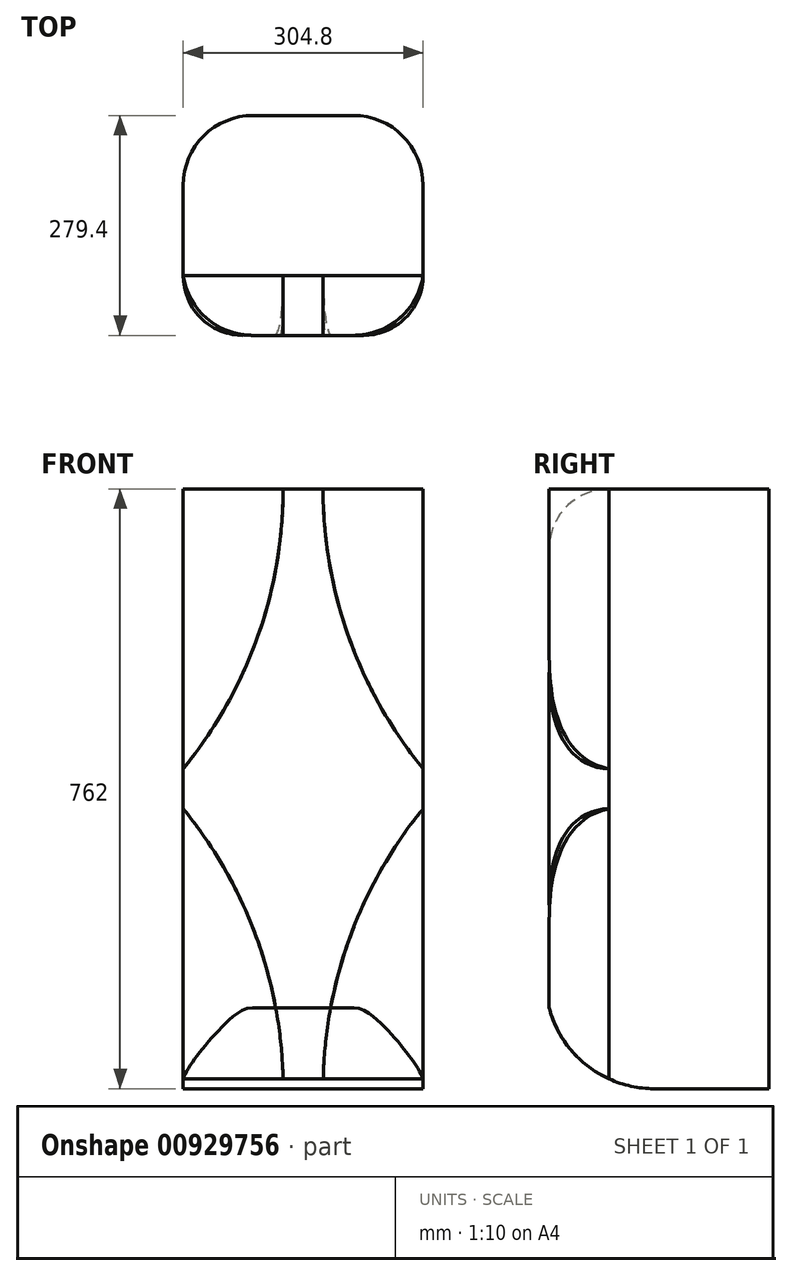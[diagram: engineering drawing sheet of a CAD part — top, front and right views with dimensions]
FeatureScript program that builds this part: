
annotation { "Feature Type Name" : "Feature", "Feature Type Description" : "" }
export const myFeature = defineFeature(function(context is Context, id is Id, definition is map)
    precondition{}
    {
        {
            var Q0;
            Q0=qCreatedBy(makeId("Front.planeOp"),FACE);
            var sketch = newSketch(context, id + "F0", { "sketchPlane" : qUnion([Q0])});
            skLineSegment(sketch, "E0.bottom", {"start": v(152.4, 381) * mm, "end": v(-152.4, 381) * mm});
            skLineSegment(sketch, "E0.top", {"start": v(152.4, -381) * mm, "end": v(-152.4, -381) * mm});
            skLineSegment(sketch, "E0.left", {"start": v(152.4, 381) * mm, "end": v(152.4, -381) * mm});
            skLineSegment(sketch, "E0.right", {"start": v(-152.4, 381) * mm, "end": v(-152.4, -381) * mm});
            skLineSegment(sketch, "E1", {"start": v(0, 0) * mm, "end": v(0, -381) * mm, "construction": true});
            skLineSegment(sketch, "E2.0", {"start": v(-25.4, 0) * mm, "end": v(-25.4, -381) * mm, "construction": true});
            skLineSegment(sketch, "E3", {"start": v(-152.4, 0) * mm, "end": v(152.4, 0) * mm});
            skLineSegment(sketch, "E4.0", {"start": v(-152.4, -25.4) * mm, "end": v(152.4, -25.4) * mm, "construction": true});
            skPoint(sketch, "E5", {"position": v(-25.4, -266.7) * mm});
            skArc(sketch, "E6", {"start": v(-25.4, -381) * mm, "mid": v(-58.1, -192.2) * mm, "end": v(-152.4, -25.4) * mm, "construction": true});
            skArc(sketch, "E7.MirrorCS", {"start": v(25.4, -381) * mm, "mid": v(58.1, -192.2) * mm, "end": v(152.4, -25.4) * mm, "construction": true});
            skArc(sketch, "E8.MirrorCS", {"start": v(25.4, 381) * mm, "mid": v(58.1, 192.2) * mm, "end": v(152.4, 25.4) * mm, "construction": true});
            skArc(sketch, "E9.MirrorCS", {"start": v(-25.4, 381) * mm, "mid": v(-58.1, 192.2) * mm, "end": v(-152.4, 25.4) * mm, "construction": true});
            skLineSegment(sketch, "E10.bottom", {"start": v(76.2, 101.6) * mm, "end": v(-76.2, 101.6) * mm, "construction": true});
            skLineSegment(sketch, "E10.top", {"start": v(76.2, -101.6) * mm, "end": v(-76.2, -101.6) * mm, "construction": true});
            skLineSegment(sketch, "E10.left", {"start": v(76.2, 101.6) * mm, "end": v(76.2, -101.6) * mm, "construction": true});
            skLineSegment(sketch, "E10.right", {"start": v(-76.2, 101.6) * mm, "end": v(-76.2, -101.6) * mm, "construction": true});
            skPoint(sketch, "E10.middle", {"position": v(0, 0) * mm});
            skSolve(sketch);
        }
        {
            var Q0;
            Q0=qCreatedBy(makeId("Top.planeOp"),FACE);
            var Q1;
            Q1=sQuery(id+"F0.wireOp",VERTEX,"E1.end");
            cPlane(context, id + "F1", {"entities" : qUnion([Q0, Q1]), "cplaneType" : CPlaneType.PLANE_POINT, "offset" : 25.4 * mm, "width" : 152.4 * mm, "height" : 152.4 * mm});
        }
        {
            var Q0;
            Q0=qCreatedBy(id+"F1.planeOp",FACE);
            var sketch = newSketch(context, id + "F2", { "sketchPlane" : qUnion([Q0])});
            skPoint(sketch, "E11.0", {"position": v(152.4, 0) * mm});
            skPoint(sketch, "E12.middle", {"position": v(0, 0) * mm});
            skPoint(sketch, "E13.0", {"position": v(-152.4, 0) * mm});
            skPoint(sketch, "E14.0", {"position": v(-25.4, 0) * mm});
            skPoint(sketch, "E15.0", {"position": v(25.4, 0) * mm});
            skLineSegment(sketch, "E16.bottom", {"start": v(-152.4, 0) * mm, "end": v(152.4, 0) * mm});
            skLineSegment(sketch, "E16.top", {"start": v(-152.4, 203.2) * mm, "end": v(152.4, 203.2) * mm});
            skLineSegment(sketch, "E16.left", {"start": v(-152.4, 0) * mm, "end": v(-152.4, 203.2) * mm});
            skLineSegment(sketch, "E16.right", {"start": v(152.4, 0) * mm, "end": v(152.4, 203.2) * mm});
            skLineSegment(sketch, "E17", {"start": v(0, 0) * mm, "end": v(0, 152.4) * mm, "construction": true});
            skSolve(sketch);
        }
        {
            var Q0;
            Q0 = qSketchRegion(id + "F2", true);
            var Q1;
            Q1=sQuery(id+"F0.wireOp",VERTEX,"E0.bottom.end");
            extrude(context, id + "F3", {"entities" : qUnion([Q0]), "endBound" : BoundingType.UP_TO_VERTEX, "depth" : 25.4 * mm, "endBoundEntityVertex" : qUnion([Q1]), "offsetDistance" : 25.4 * mm});
        }
        {
            var Q0;
            Q0=qCreatedBy(makeId("Top.planeOp"),FACE);
            var sketch = newSketch(context, id + "F4", { "sketchPlane" : qUnion([Q0])});
            skCircle(sketch, "E18.0", {"center": v(0, 0) * mm, "radius": 76.2 * mm, "construction": true});
            skLineSegment(sketch, "E19", {"start": v(0, 0) * mm, "end": v(0, -76.2) * mm, "construction": true});
            skPoint(sketch, "E20", {"position": v(0, -76.2) * mm});
            skSolve(sketch);
        }
        {
            var Q0;
            Q0=sQuery(id+"F4.wireOp",VERTEX,"E20");
            var Q1;
            Q1=qCreatedBy(makeId("Front.planeOp"),FACE);
            cPlane(context, id + "F5", {"entities" : qUnion([Q0, Q1]), "cplaneType" : CPlaneType.PLANE_POINT, "offset" : 25.4 * mm, "width" : 152.4 * mm, "height" : 152.4 * mm});
        }
        {
            var Q0;
            Q0=qCreatedBy(id+"F5.planeOp",FACE);
            var sketch = newSketch(context, id + "F6", { "sketchPlane" : qUnion([Q0])});
            skLineSegment(sketch, "E21.0", {"start": v(152.4, 381) * mm, "end": v(25.4, 381) * mm});
            skLineSegment(sketch, "E21.1", {"start": v(152.4, -381) * mm, "end": v(25.4, -381) * mm});
            skLineSegment(sketch, "E21.2", {"start": v(152.4, 381) * mm, "end": v(152.4, 25.4) * mm});
            skLineSegment(sketch, "E21.3", {"start": v(-152.4, 381) * mm, "end": v(-152.4, 25.4) * mm});
            skPoint(sketch, "E21.11", {"position": v(-25.4, -266.7) * mm});
            skArc(sketch, "E21.12", {"start": v(-25.4, -381) * mm, "mid": v(-58.1, -192.2) * mm, "end": v(-152.4, -25.4) * mm});
            skArc(sketch, "E21.13", {"start": v(25.4, -381) * mm, "mid": v(58.1, -192.2) * mm, "end": v(152.4, -25.4) * mm});
            skArc(sketch, "E21.14", {"start": v(25.4, 381) * mm, "mid": v(58.1, 192.2) * mm, "end": v(152.4, 25.4) * mm});
            skArc(sketch, "E21.15", {"start": v(-25.4, 381) * mm, "mid": v(-58.1, 192.2) * mm, "end": v(-152.4, 25.4) * mm});
            skLineSegment(sketch, "E21.16", {"start": v(76.2, 101.6) * mm, "end": v(-76.2, 101.6) * mm});
            skLineSegment(sketch, "E21.17", {"start": v(76.2, -101.6) * mm, "end": v(-76.2, -101.6) * mm});
            skLineSegment(sketch, "E21.18", {"start": v(76.2, 101.6) * mm, "end": v(76.2, -101.6) * mm});
            skLineSegment(sketch, "E21.19", {"start": v(-76.2, 101.6) * mm, "end": v(-76.2, -101.6) * mm});
            skPoint(sketch, "E21.20", {"position": v(0, 0) * mm});
            skLineSegment(sketch, "E22.trimOffspring", {"start": v(-25.4, 381) * mm, "end": v(-152.4, 381) * mm});
            skLineSegment(sketch, "E23.trimOffspring", {"start": v(-25.4, -381) * mm, "end": v(-152.4, -381) * mm});
            skLineSegment(sketch, "E24.trimOffspring", {"start": v(152.4, -25.4) * mm, "end": v(152.4, -381) * mm});
            skLineSegment(sketch, "E25.trimOffspring", {"start": v(-152.4, -25.4) * mm, "end": v(-152.4, -381) * mm});
            skSolve(sketch);
        }
        {
            var Q0;
            Q0=makeQuery(id+"F6.imprint","IMPRINT",FACE,{"disambiguationData":[TD([[makeQuery(id+"F6.imprint","IMPRINT",EDGE,{"derivedFrom":sQuery(id+"F6.wireOp",EDGE,"E21.3")}),1.0]])]});
            var Q1;
            Q1=makeQuery(id+"F6.imprint","IMPRINT",FACE,{"disambiguationData":[TD([[makeQuery(id+"F6.imprint","IMPRINT",EDGE,{"derivedFrom":sQuery(id+"F6.wireOp",EDGE,"E21.0")}),1.0]])]});
            var Q2;
            Q2=makeQuery(id+"F6.imprint","IMPRINT",FACE,{"disambiguationData":[TD([[makeQuery(id+"F6.imprint","IMPRINT",EDGE,{"derivedFrom":sQuery(id+"F6.wireOp",EDGE,"E21.1")}),-1.0]])]});
            var Q3;
            Q3=makeQuery(id+"F6.imprint","IMPRINT",FACE,{"disambiguationData":[TD([[makeQuery(id+"F6.imprint","IMPRINT",EDGE,{"derivedFrom":sQuery(id+"F6.wireOp",EDGE,"E21.12")}),1.0]])]});
            extrude(context, id + "F7", {"entities" : qUnion([Q0, Q1, Q2, Q3]), "endBound" : BoundingType.UP_TO_NEXT, "oppositeDirection" : true, "depth" : 25.4 * mm, "offsetDistance" : 25.4 * mm});
        }
        {
            var Q0;
            Q0=makeQuery(id+"F7.opExtrude","CAP_EDGE",EDGE,{"disambiguationData":[OSD([sQuery(id+"F6.wireOp",EDGE,"E21.2")])],"isStart":true});
            var Q1;
            Q1=makeQuery(id+"F7.opExtrude","CAP_EDGE",EDGE,{"disambiguationData":[OSD([sQuery(id+"F6.wireOp",EDGE,"E21.3")])],"isStart":true});
            var Q2;
            Q2=makeQuery(id+"F7.opExtrude","CAP_EDGE",EDGE,{"disambiguationData":[OSD([sQuery(id+"F6.wireOp",EDGE,"E25.trimOffspring")])],"isStart":true});
            var Q3;
            Q3=makeQuery(id+"F7.opExtrude","CAP_EDGE",EDGE,{"disambiguationData":[OSD([sQuery(id+"F6.wireOp",EDGE,"E24.trimOffspring")])],"isStart":true});
            var Q4;
            Q4=makeQuery(id+"F3.opExtrude","SWEPT_EDGE",EDGE,{"disambiguationData":[OSD([sQuery(id+"F2.wireOp",EDGE,"E16.top"),sQuery(id+"F2.wireOp",EDGE,"E16.right")])]});
            var Q5;
            Q5=makeQuery(id+"F3.opExtrude","SWEPT_EDGE",EDGE,{"disambiguationData":[OSD([sQuery(id+"F2.wireOp",EDGE,"E16.top"),sQuery(id+"F2.wireOp",EDGE,"E16.left")])]});
            fillet(context, id + "F8", {"entities" : qUnion([Q0, Q1, Q2, Q3, Q4, Q5]), "radius" : 88.9 * mm, "tangentPropagation" : true, "allowEdgeOverflow" : false});
        }
        {
            var Q0;
            Q0=makeQuery(id+"F3.opExtrude","SWEPT_FACE",FACE,{"disambiguationData":[OSD([sQuery(id+"F2.wireOp",EDGE,"E16.bottom")])]});
            var sketch = newSketch(context, id + "F9", { "sketchPlane" : qUnion([Q0])});
            skArc(sketch, "E26.0", {"start": v(-152.4, 25.4) * mm, "mid": v(-102.56, 96.97) * mm, "end": v(-64.41, 175.39) * mm});
            skArc(sketch, "E27.0", {"start": v(-25.4, 381) * mm, "mid": v(-35.24, 276.36) * mm, "end": v(-64.41, 175.39) * mm});
            skArc(sketch, "E28.0", {"start": v(25.4, 381) * mm, "mid": v(35.24, 276.36) * mm, "end": v(64.41, 175.39) * mm});
            skArc(sketch, "E29.0", {"start": v(64.41, 175.39) * mm, "mid": v(102.56, 96.97) * mm, "end": v(152.4, 25.4) * mm});
            skArc(sketch, "E30.0", {"start": v(152.4, -25.4) * mm, "mid": v(102.56, -96.97) * mm, "end": v(64.41, -175.39) * mm});
            skArc(sketch, "E31.0", {"start": v(25.4, -381) * mm, "mid": v(35.24, -276.36) * mm, "end": v(64.41, -175.39) * mm});
            skArc(sketch, "E32.0", {"start": v(-25.4, -381) * mm, "mid": v(-35.24, -276.36) * mm, "end": v(-64.41, -175.39) * mm});
            skArc(sketch, "E33.0", {"start": v(-64.41, -175.39) * mm, "mid": v(-102.56, -96.97) * mm, "end": v(-152.4, -25.4) * mm});
            skLineSegment(sketch, "E34", {"start": v(-152.4, 25.4) * mm, "end": v(-152.4, -25.4) * mm});
            skLineSegment(sketch, "E35", {"start": v(152.4, 25.4) * mm, "end": v(152.4, -25.4) * mm});
            skLineSegment(sketch, "E36", {"start": v(-25.4, 381) * mm, "end": v(25.4, 381) * mm});
            skLineSegment(sketch, "E37", {"start": v(-25.4, -381) * mm, "end": v(25.4, -381) * mm});
            skSolve(sketch);
        }
        {
            var Q0;
            Q0 = qSketchRegion(id + "F9", true);
            var Q1;
            Q1=makeQuery(id+"F7.opExtrude","CAP_VERTEX",VERTEX,{"disambiguationData":[OSD([sQuery(id+"F6.wireOp",EDGE,"E21.15"),sQuery(id+"F6.wireOp",EDGE,"E22.trimOffspring")])],"isStart":true});
            extrude(context, id + "F10", {"entities" : qUnion([Q0]), "endBound" : BoundingType.UP_TO_VERTEX, "depth" : 25.4 * mm, "endBoundEntityVertex" : qUnion([Q1]), "offsetDistance" : 25.4 * mm});
        }
        {
            var Q0;
            Q0=makeQuery(id+"F10.opExtrude","CAP_EDGE",EDGE,{"disambiguationData":[OSD([sQuery(id+"F9.wireOp",EDGE,"E34")])],"isStart":false});
            var Q1;
            Q1=makeQuery(id+"F10.opExtrude","CAP_EDGE",EDGE,{"disambiguationData":[OSD([sQuery(id+"F9.wireOp",EDGE,"E35")])],"isStart":false});
            fillet(context, id + "F11", {"entities" : qUnion([Q0, Q1]), "radius" : 76.2 * mm, "tangentPropagation" : true, "allowEdgeOverflow" : false});
        }
        {
            var Q0;
            Q0=makeQuery(id+"F10.opExtrude","CAP_EDGE",EDGE,{"disambiguationData":[OSD([sQuery(id+"F9.wireOp",EDGE,"E36")])],"isStart":false});
            fillet(context, id + "F12", {"entities" : qUnion([Q0]), "radius" : 76.2 * mm, "tangentPropagation" : true, "allowEdgeOverflow" : false});
        }
        {
            var Q0;
            Q0=qCreatedBy(makeId("Right.planeOp"),FACE);
            var sketch = newSketch(context, id + "F13", { "sketchPlane" : qUnion([Q0])});
            skPoint(sketch, "E38.0", {"position": v(57.15, -381) * mm});
            skPoint(sketch, "E39.0", {"position": v(-76.2, -278.2) * mm});
            skLineSegment(sketch, "E40", {"start": v(-76.2, -278.2) * mm, "end": v(-76.2, -381) * mm});
            skLineSegment(sketch, "E41", {"start": v(57.15, -381) * mm, "end": v(-76.2, -381) * mm});
            skArc(sketch, "E42", {"start": v(-76.2, -278.2) * mm, "mid": v(-27.04, -352.31) * mm, "end": v(57.15, -381) * mm});
            skSolve(sketch);
        }
        {
            var Q0;
            Q0 = qSketchRegion(id + "F13", true);
            extrude(context, id + "F14", {"entities" : qUnion([Q0]), "operationType" : NewBodyOperationType.REMOVE, "endBound" : BoundingType.THROUGH_ALL, "oppositeDirection" : true, "depth" : 25.4 * mm, "offsetDistance" : 25.4 * mm, "hasSecondDirection" : true, "secondDirectionBound" : BoundingType.THROUGH_ALL, "secondDirectionOppositeDirection" : false, "secondDirectionDepth" : 25.4 * mm});
        }
    });
